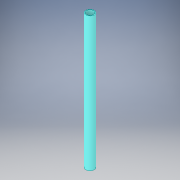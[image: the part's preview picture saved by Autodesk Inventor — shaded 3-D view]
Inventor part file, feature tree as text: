
AUTODESK INVENTOR PART (.ipt)
format: ipt  version: 2018 (Build 220112000, 112)  size: 105,472 bytes
history: native  units: in
note: dims shown in document units (in); Inventor stores cm internally (conversion verified against a paired STEP export)
features: extrude x1, sketch x1
ambient origin geometry x8: Origin, YZ Plane, XZ Plane, XY Plane, X Axis, Y Axis, Z Axis, Center Point
bodies: Solid1 (feature_tree)
feature tree (2):
  extrude  "Extrusion1"  Depth=6.0in
  sketch  "Sketch1"  dims[d0=0.375in d1=0.31in d2=6.0in d3=0.0in]
